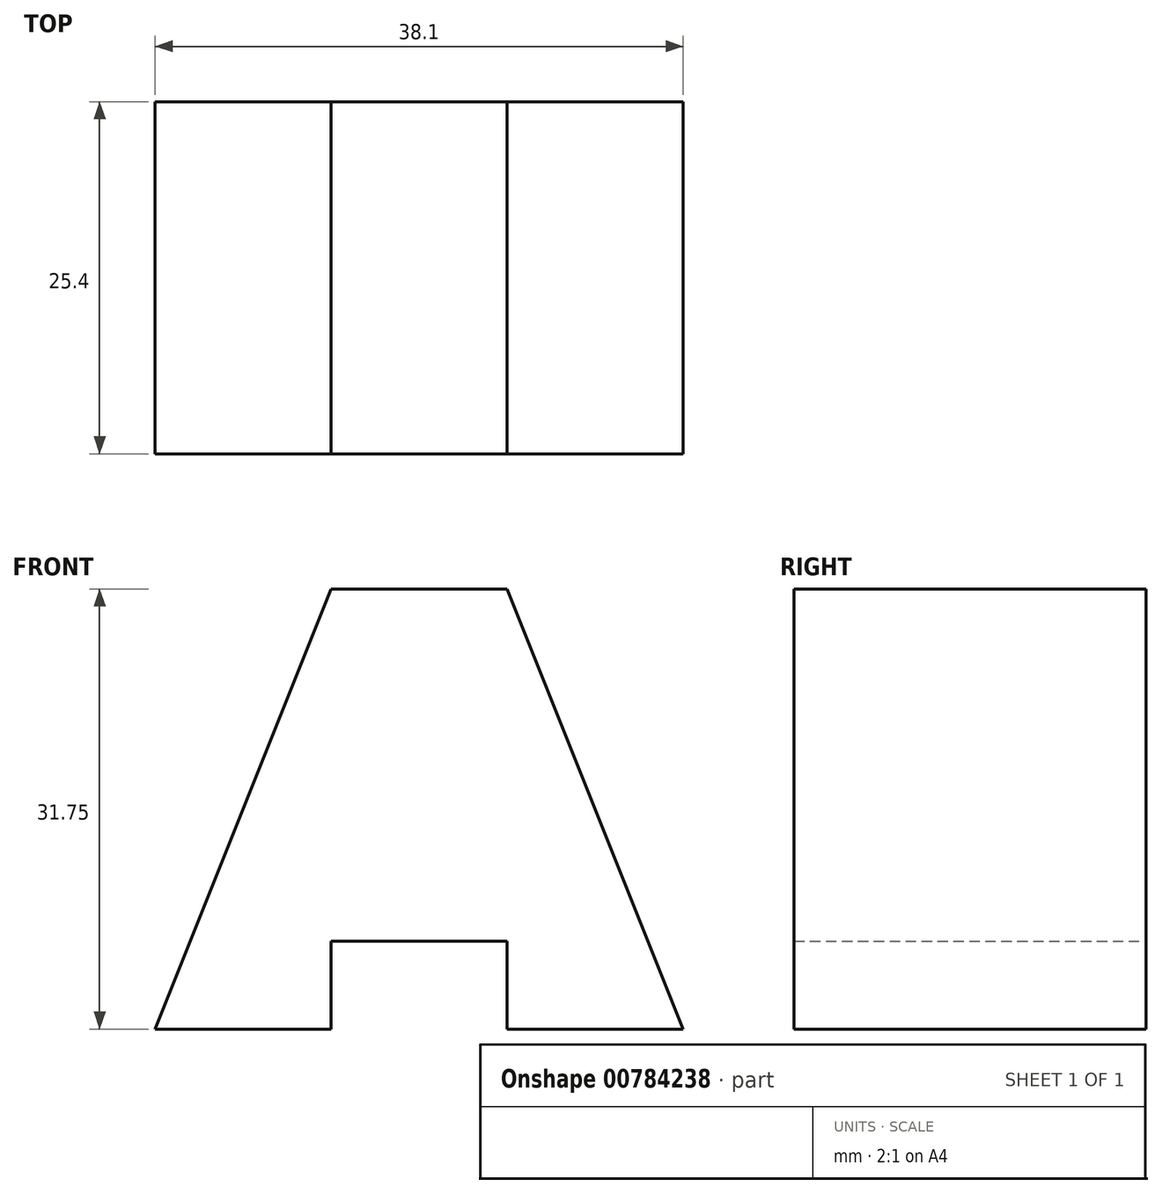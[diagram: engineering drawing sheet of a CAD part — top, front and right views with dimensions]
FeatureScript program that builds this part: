
annotation { "Feature Type Name" : "Feature", "Feature Type Description" : "" }
export const myFeature = defineFeature(function(context is Context, id is Id, definition is map)
    precondition{}
    {
        {
            var Q0;
            Q0=qCreatedBy(makeId("Front.planeOp"),FACE);
            var sketch = newSketch(context, id + "F0", { "sketchPlane" : qUnion([Q0])});
            skLineSegment(sketch, "E0", {"start": v(0, 0) * mm, "end": v(12.7, 0) * mm});
            skLineSegment(sketch, "E1", {"start": v(12.7, 0) * mm, "end": v(12.7, 6.35) * mm});
            skLineSegment(sketch, "E2", {"start": v(12.7, 6.35) * mm, "end": v(25.4, 6.35) * mm});
            skLineSegment(sketch, "E3", {"start": v(25.4, 6.35) * mm, "end": v(25.4, 0) * mm});
            skLineSegment(sketch, "E4", {"start": v(25.4, 0) * mm, "end": v(38.1, 0) * mm});
            skLineSegment(sketch, "E5", {"start": v(0, 0) * mm, "end": v(0, 31.75) * mm});
            skLineSegment(sketch, "E6", {"start": v(0, 31.75) * mm, "end": v(38.1, 31.75) * mm});
            skLineSegment(sketch, "E7", {"start": v(38.1, 31.75) * mm, "end": v(38.1, 0) * mm});
            skLineSegment(sketch, "E8", {"start": v(38.1, 31.75) * mm, "end": v(25.4, 31.75) * mm});
            skLineSegment(sketch, "E9", {"start": v(25.4, 31.75) * mm, "end": v(12.7, 31.75) * mm});
            skLineSegment(sketch, "E10", {"start": v(12.7, 31.75) * mm, "end": v(0, 0) * mm});
            skLineSegment(sketch, "E11", {"start": v(25.4, 31.75) * mm, "end": v(38.1, 0) * mm});
            skLineSegment(sketch, "E12", {"start": v(30.5, 22.8) * mm, "end": v(32.44, 24.87) * mm});
            skSolve(sketch);
        }
        {
            var Q0;
            Q0=makeQuery(id+"F0.imprint","IMPRINT",FACE,{"disambiguationData":[TD([[makeQuery(id+"F0.imprint","IMPRINT",EDGE,{"derivedFrom":sQuery(id+"F0.wireOp",EDGE,"E0")}),1.0]])]});
            extrude(context, id + "F1", {"entities" : qUnion([Q0]), "depth" : 25.4 * mm, "offsetDistance" : 25.4 * mm});
        }
    });
